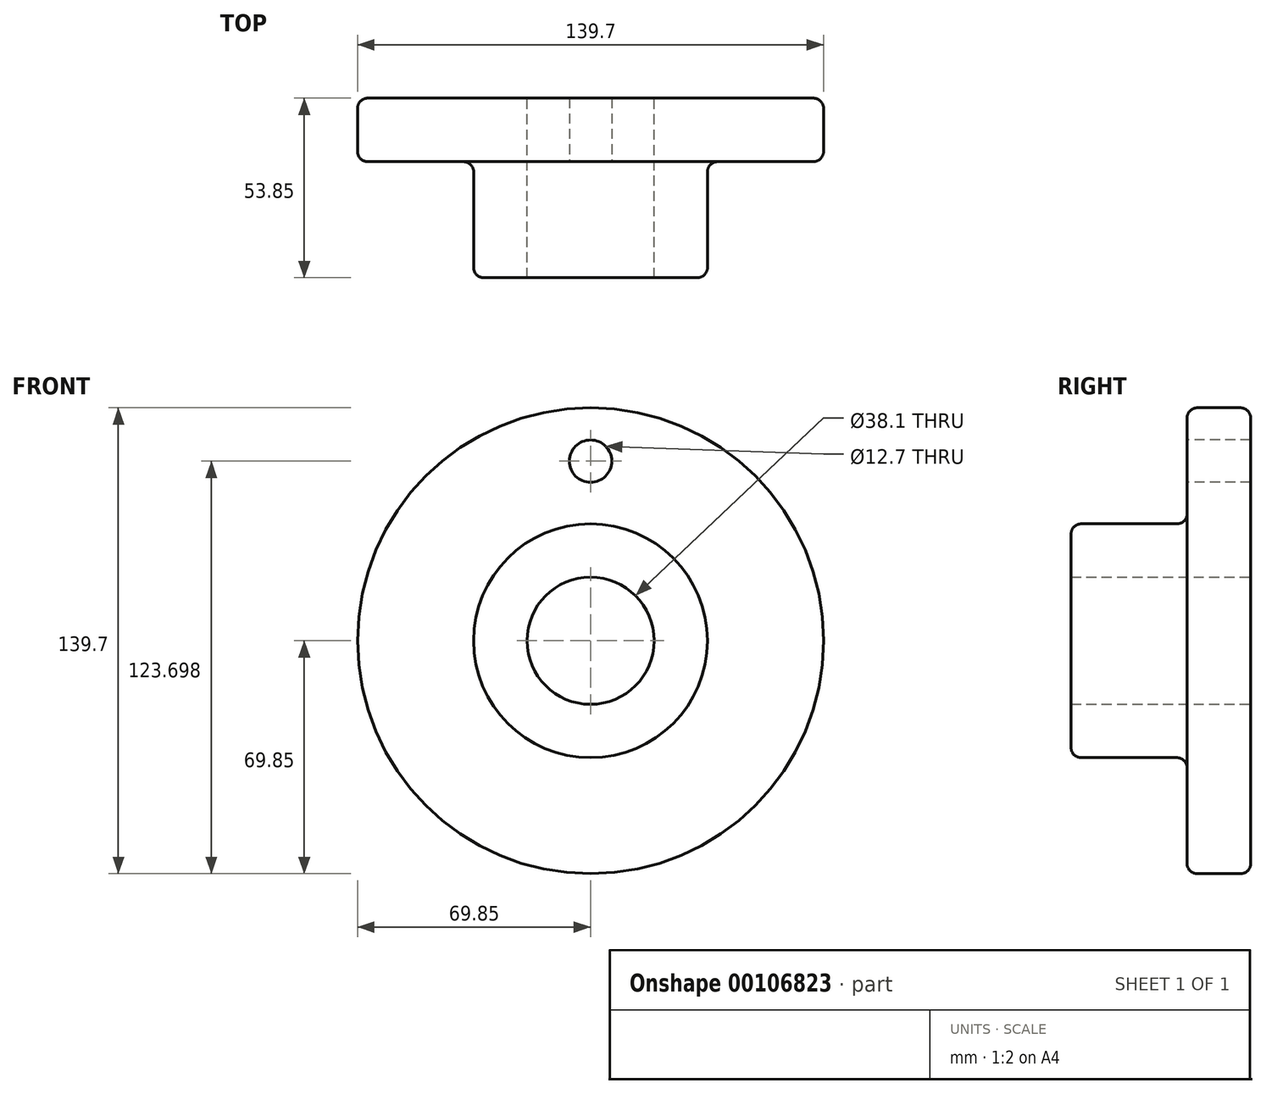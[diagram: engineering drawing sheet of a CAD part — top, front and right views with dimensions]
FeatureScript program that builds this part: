
annotation { "Feature Type Name" : "Feature", "Feature Type Description" : "" }
export const myFeature = defineFeature(function(context is Context, id is Id, definition is map)
    precondition{}
    {
        {
            var Q0;
            Q0=qCreatedBy(makeId("Right.planeOp"),FACE);
            var sketch = newSketch(context, id + "F0", { "sketchPlane" : qUnion([Q0])});
            skLineSegment(sketch, "E0", {"start": v(0, 0) * mm, "end": v(0, 19.05) * mm, "construction": true});
            skLineSegment(sketch, "E1", {"start": v(0, 19.05) * mm, "end": v(-53.85, 19.05) * mm});
            skLineSegment(sketch, "E2", {"start": v(-53.85, 19.05) * mm, "end": v(-53.85, 35.05) * mm});
            skLineSegment(sketch, "E3", {"start": v(-53.85, 35.05) * mm, "end": v(-19.05, 35.05) * mm});
            skLineSegment(sketch, "E4", {"start": v(-19.05, 35.05) * mm, "end": v(-19.05, 69.85) * mm});
            skLineSegment(sketch, "E5", {"start": v(-19.05, 69.85) * mm, "end": v(0, 69.85) * mm});
            skLineSegment(sketch, "E6", {"start": v(0, 69.85) * mm, "end": v(0, 19.05) * mm});
            skLineSegment(sketch, "E7", {"start": v(0, 0) * mm, "end": v(-60.33, 0) * mm, "construction": true});
            skSolve(sketch);
        }
        {
            var Q0;
            Q0 = qSketchRegion(id + "F0", true);
            var Q1;
            Q1=sQuery(id+"F0.wireOp",EDGE,"E7");
            revolve(context, id + "F1", {"entities" : qUnion([Q0]), "axis" : qUnion([Q1]), "revolveType" : RevolveType.FULL});
        }
        {
            var Q0;
            Q0=makeQuery(id+"F1.opRevolve","SWEPT_EDGE",EDGE,{"disambiguationData":[OSD([sQuery(id+"F0.wireOp",EDGE,"E2"),sQuery(id+"F0.wireOp",EDGE,"E3")])]});
            var Q1;
            Q1=makeQuery(id+"F1.opRevolve","SWEPT_EDGE",EDGE,{"disambiguationData":[OSD([sQuery(id+"F0.wireOp",EDGE,"E3"),sQuery(id+"F0.wireOp",EDGE,"E4")])]});
            var Q2;
            Q2=makeQuery(id+"F1.opRevolve","SWEPT_EDGE",EDGE,{"disambiguationData":[OSD([sQuery(id+"F0.wireOp",EDGE,"E4"),sQuery(id+"F0.wireOp",EDGE,"E5")])]});
            var Q3;
            Q3=makeQuery(id+"F1.opRevolve","SWEPT_EDGE",EDGE,{"disambiguationData":[OSD([sQuery(id+"F0.wireOp",EDGE,"E5"),sQuery(id+"F0.wireOp",EDGE,"E6")])]});
            fillet(context, id + "F2", {"entities" : qUnion([Q0, Q1, Q2, Q3]), "radius" : 3.05 * mm, "tangentPropagation" : true, "allowEdgeOverflow" : false});
        }
        {
            var Q0;
            Q0=makeQuery(id+"F1.opRevolve","SWEPT_FACE",FACE,{"disambiguationData":[OSD([sQuery(id+"F0.wireOp",EDGE,"E4")])]});
            var sketch = newSketch(context, id + "F3", { "sketchPlane" : qUnion([Q0])});
            skLineSegment(sketch, "E8", {"start": v(0, 0) * mm, "end": v(0, 53.85) * mm, "construction": true});
            skCircle(sketch, "E9", {"center": v(0, 53.85) * mm, "radius": 6.35 * mm});
            skSolve(sketch);
        }
        {
            var Q0;
            Q0 = qSketchRegion(id + "F3", true);
            extrude(context, id + "F4", {"entities" : qUnion([Q0]), "operationType" : NewBodyOperationType.REMOVE, "endBound" : BoundingType.THROUGH_ALL, "oppositeDirection" : true, "depth" : 25.4 * mm});
        }
    });
